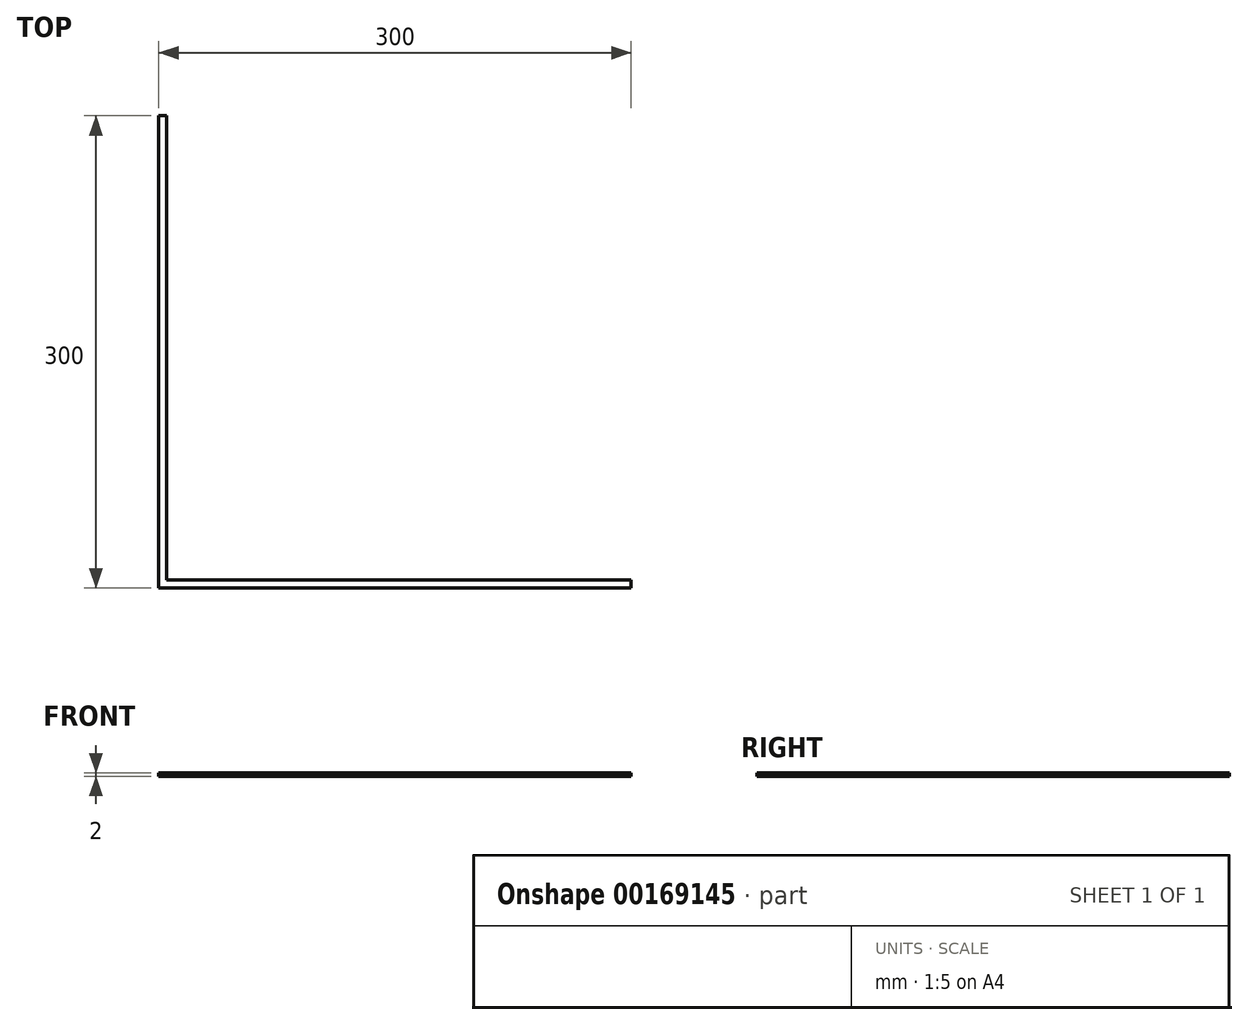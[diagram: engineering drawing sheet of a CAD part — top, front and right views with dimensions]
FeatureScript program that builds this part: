
annotation { "Feature Type Name" : "Feature", "Feature Type Description" : "" }
export const myFeature = defineFeature(function(context is Context, id is Id, definition is map)
    precondition{}
    {
        {
            var Q0;
            Q0=qCreatedBy(makeId("Top.planeOp"),FACE);
            var sketch = newSketch(context, id + "F0", { "sketchPlane" : qUnion([Q0])});
            skLineSegment(sketch, "E0.bottom", {"start": v(0, 0) * mm, "end": v(5, 0) * mm});
            skLineSegment(sketch, "E0.top", {"start": v(0, 300) * mm, "end": v(5, 300) * mm});
            skLineSegment(sketch, "E0.left", {"start": v(0, 0) * mm, "end": v(0, 300) * mm});
            skLineSegment(sketch, "E0.right", {"start": v(5, 0) * mm, "end": v(5, 300) * mm});
            skLineSegment(sketch, "E1.bottom", {"start": v(0, 0) * mm, "end": v(300, 0) * mm});
            skLineSegment(sketch, "E1.top", {"start": v(0, 5) * mm, "end": v(300, 5) * mm});
            skLineSegment(sketch, "E1.left", {"start": v(0, 0) * mm, "end": v(0, 5) * mm});
            skLineSegment(sketch, "E1.right", {"start": v(300, 0) * mm, "end": v(300, 5) * mm});
            skSolve(sketch);
        }
        {
            var Q0;
            Q0 = qSketchRegion(id + "F0", true);
            extrude(context, id + "F1", {"entities" : qUnion([Q0]), "depth" : 2 * mm});
        }
    });
